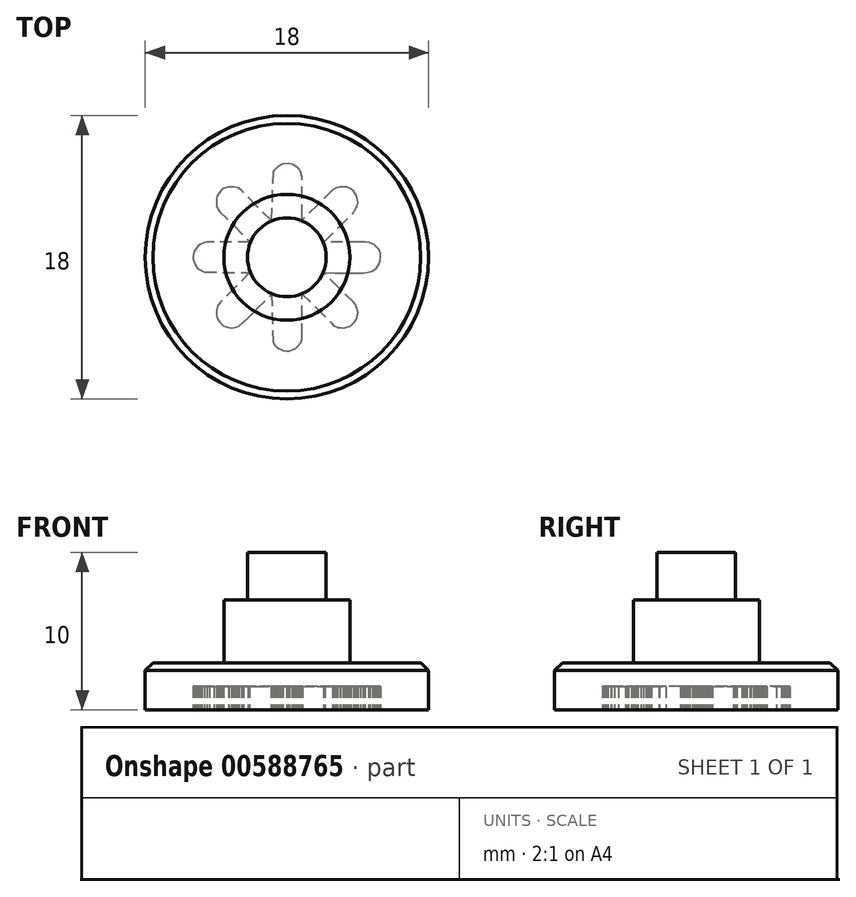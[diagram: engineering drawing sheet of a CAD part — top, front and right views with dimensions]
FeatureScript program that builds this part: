
annotation { "Feature Type Name" : "Feature", "Feature Type Description" : "" }
export const myFeature = defineFeature(function(context is Context, id is Id, definition is map)
    precondition{}
    {
        {
            var Q0;
            Q0=qCreatedBy(makeId("Top.planeOp"),FACE);
            var sketch = newSketch(context, id + "F0", { "sketchPlane" : qUnion([Q0])});
            skCircle(sketch, "E0", {"center": v(0, 0) * mm, "radius": 9 * mm});
            skSolve(sketch);
        }
        {
            var Q0;
            Q0=makeQuery(id+"F0.imprint","IMPRINT",FACE,{"disambiguationData":[TD([[makeQuery(id+"F0.imprint","IMPRINT",EDGE,{"derivedFrom":sQuery(id+"F0.wireOp",EDGE,"E0")}),1.0]])]});
            extrude(context, id + "F1", {"entities" : qUnion([Q0]), "depth" : 3 * mm, "offsetDistance" : 25 * mm});
        }
        {
            var Q0;
            Q0=makeQuery(id+"F1.opExtrude","CAP_EDGE",EDGE,{"disambiguationData":[OSD([sQuery(id+"F0.wireOp",EDGE,"E0")])],"isStart":false});
            chamfer(context, id + "F2", {"entities" : qUnion([Q0]), "width" : .5 * mm, "tangentPropagation" : true});
        }
        {
            var Q0;
            Q0=makeQuery(id+"F1.opExtrude","CAP_FACE",FACE,{"disambiguationData":[OSD([sQuery(id+"F0.wireOp",EDGE,"E0")])],"isStart":false});
            var sketch = newSketch(context, id + "F3", { "sketchPlane" : qUnion([Q0])});
            skCircle(sketch, "E1", {"center": v(0, 0) * mm, "radius": 4 * mm});
            skSolve(sketch);
        }
        {
            var Q0;
            Q0=qSketchRegion(id+"F3",true);
            extrude(context, id + "F4", {"entities" : qUnion([Q0]), "operationType" : NewBodyOperationType.ADD, "depth" : 4 * mm, "offsetDistance" : 25 * mm});
        }
        {
            var Q0;
            Q0=makeQuery(id+"F4.opExtrude","CAP_FACE",FACE,{"disambiguationData":[OSD([sQuery(id+"F3.wireOp",EDGE,"E1")])],"isStart":false});
            var sketch = newSketch(context, id + "F5", { "sketchPlane" : qUnion([Q0])});
            skCircle(sketch, "E2", {"center": v(0, 0) * mm, "radius": 2.5 * mm});
            skSolve(sketch);
        }
        {
            var Q0;
            Q0=qSketchRegion(id+"F5",true);
            extrude(context, id + "F6", {"entities" : qUnion([Q0]), "operationType" : NewBodyOperationType.ADD, "depth" : 3 * mm, "offsetDistance" : 25 * mm});
        }
        {
            var Q0;
            Q0=makeQuery(id+"F1.opExtrude","CAP_FACE",FACE,{"disambiguationData":[OSD([sQuery(id+"F0.wireOp",EDGE,"E0")])],"isStart":true});
            var sketch = newSketch(context, id + "F7", { "sketchPlane" : qUnion([Q0])});
            skLineSegment(sketch, "E3", {"start": v(-0.24, 5.92) * mm, "end": v(-0.03, 5.95) * mm});
            skLineSegment(sketch, "E4", {"start": v(-0.03, 5.95) * mm, "end": v(0.18, 5.95) * mm});
            skLineSegment(sketch, "E5", {"start": v(0.18, 5.95) * mm, "end": v(0.31, 5.9) * mm});
            skLineSegment(sketch, "E6", {"start": v(0.31, 5.9) * mm, "end": v(0.44, 5.83) * mm});
            skLineSegment(sketch, "E7", {"start": v(0.44, 5.83) * mm, "end": v(0.47, 5.81) * mm});
            skLineSegment(sketch, "E8", {"start": v(0.47, 5.81) * mm, "end": v(0.5, 5.8) * mm});
            skLineSegment(sketch, "E9", {"start": v(0.5, 5.8) * mm, "end": v(0.54, 5.8) * mm});
            skLineSegment(sketch, "E10", {"start": v(0.54, 5.8) * mm, "end": v(0.58, 5.77) * mm});
            skLineSegment(sketch, "E11", {"start": v(0.58, 5.77) * mm, "end": v(0.65, 5.71) * mm});
            skLineSegment(sketch, "E12", {"start": v(0.65, 5.71) * mm, "end": v(0.89, 5.42) * mm});
            skLineSegment(sketch, "E13", {"start": v(0.89, 5.42) * mm, "end": v(0.95, 5.19) * mm});
            skLineSegment(sketch, "E14", {"start": v(0.95, 5.19) * mm, "end": v(0.97, 4.95) * mm});
            skLineSegment(sketch, "E15", {"start": v(0.97, 4.95) * mm, "end": v(0.97, 3.1) * mm});
            skLineSegment(sketch, "E16", {"start": v(0.97, 3.1) * mm, "end": v(0.97, 2.33) * mm});
            skLineSegment(sketch, "E17", {"start": v(0.97, 2.33) * mm, "end": v(1.92, 3.27) * mm});
            skLineSegment(sketch, "E18", {"start": v(1.92, 3.27) * mm, "end": v(2.86, 4.21) * mm});
            skLineSegment(sketch, "E19", {"start": v(2.86, 4.21) * mm, "end": v(2.94, 4.3) * mm});
            skLineSegment(sketch, "E20", {"start": v(2.94, 4.3) * mm, "end": v(3.04, 4.36) * mm});
            skLineSegment(sketch, "E21", {"start": v(3.04, 4.36) * mm, "end": v(3.19, 4.42) * mm});
            skLineSegment(sketch, "E22", {"start": v(3.19, 4.42) * mm, "end": v(3.22, 4.45) * mm});
            skLineSegment(sketch, "E23", {"start": v(3.22, 4.45) * mm, "end": v(3.4, 4.48) * mm});
            skLineSegment(sketch, "E24", {"start": v(3.4, 4.48) * mm, "end": v(3.56, 4.48) * mm});
            skLineSegment(sketch, "E25", {"start": v(3.56, 4.48) * mm, "end": v(3.72, 4.48) * mm});
            skLineSegment(sketch, "E26", {"start": v(3.72, 4.48) * mm, "end": v(4.04, 4.36) * mm});
            skLineSegment(sketch, "E27", {"start": v(4.04, 4.36) * mm, "end": v(4.3, 4.12) * mm});
            skLineSegment(sketch, "E28", {"start": v(4.3, 4.12) * mm, "end": v(4.39, 3.98) * mm});
            skLineSegment(sketch, "E29", {"start": v(4.39, 3.98) * mm, "end": v(4.44, 3.83) * mm});
            skLineSegment(sketch, "E30", {"start": v(4.44, 3.83) * mm, "end": v(4.51, 3.5) * mm});
            skLineSegment(sketch, "E31", {"start": v(4.51, 3.5) * mm, "end": v(4.45, 3.2) * mm});
            skLineSegment(sketch, "E32", {"start": v(4.45, 3.2) * mm, "end": v(4.4, 3.12) * mm});
            skLineSegment(sketch, "E33", {"start": v(4.4, 3.12) * mm, "end": v(4.38, 3.05) * mm});
            skLineSegment(sketch, "E34", {"start": v(4.38, 3.05) * mm, "end": v(4.34, 2.98) * mm});
            skLineSegment(sketch, "E35", {"start": v(4.34, 2.98) * mm, "end": v(4.22, 2.86) * mm});
            skLineSegment(sketch, "E36", {"start": v(4.22, 2.86) * mm, "end": v(3.27, 1.91) * mm});
            skLineSegment(sketch, "E37", {"start": v(3.27, 1.91) * mm, "end": v(2.33, 0.97) * mm});
            skLineSegment(sketch, "E38", {"start": v(2.33, 0.97) * mm, "end": v(3.05, 0.98) * mm});
            skLineSegment(sketch, "E39", {"start": v(3.05, 0.98) * mm, "end": v(3.77, 1.01) * mm});
            skLineSegment(sketch, "E40", {"start": v(3.77, 1.01) * mm, "end": v(4.48, 1.01) * mm});
            skLineSegment(sketch, "E41", {"start": v(4.48, 1.01) * mm, "end": v(4.84, 0.99) * mm});
            skLineSegment(sketch, "E42", {"start": v(4.84, 0.99) * mm, "end": v(5.2, 0.94) * mm});
            skLineSegment(sketch, "E43", {"start": v(5.2, 0.94) * mm, "end": v(5.43, 0.88) * mm});
            skLineSegment(sketch, "E44", {"start": v(5.43, 0.88) * mm, "end": v(5.6, 0.74) * mm});
            skLineSegment(sketch, "E45", {"start": v(5.6, 0.74) * mm, "end": v(5.69, 0.67) * mm});
            skLineSegment(sketch, "E46", {"start": v(5.69, 0.67) * mm, "end": v(5.76, 0.6) * mm});
            skLineSegment(sketch, "E47", {"start": v(5.76, 0.6) * mm, "end": v(5.87, 0.41) * mm});
            skLineSegment(sketch, "E48", {"start": v(5.87, 0.41) * mm, "end": v(5.93, 0.23) * mm});
            skLineSegment(sketch, "E49", {"start": v(5.93, 0.23) * mm, "end": v(5.96, 0.04) * mm});
            skLineSegment(sketch, "E50", {"start": v(5.96, 0.04) * mm, "end": v(5.95, -0.15) * mm});
            skLineSegment(sketch, "E51", {"start": v(5.95, -0.15) * mm, "end": v(5.93, -0.24) * mm});
            skLineSegment(sketch, "E52", {"start": v(5.93, -0.24) * mm, "end": v(5.9, -0.32) * mm});
            skLineSegment(sketch, "E53", {"start": v(5.9, -0.32) * mm, "end": v(5.88, -0.4) * mm});
            skLineSegment(sketch, "E54", {"start": v(5.88, -0.4) * mm, "end": v(5.84, -0.48) * mm});
            skLineSegment(sketch, "E55", {"start": v(5.84, -0.48) * mm, "end": v(5.72, -0.62) * mm});
            skLineSegment(sketch, "E56", {"start": v(5.72, -0.62) * mm, "end": v(5.55, -0.82) * mm});
            skLineSegment(sketch, "E57", {"start": v(5.55, -0.82) * mm, "end": v(5.28, -0.91) * mm});
            skLineSegment(sketch, "E58", {"start": v(5.28, -0.91) * mm, "end": v(5.25, -0.94) * mm});
            skLineSegment(sketch, "E59", {"start": v(5.25, -0.94) * mm, "end": v(4.97, -0.97) * mm});
            skLineSegment(sketch, "E60", {"start": v(4.97, -0.97) * mm, "end": v(4.7, -0.97) * mm});
            skLineSegment(sketch, "E61", {"start": v(4.7, -0.97) * mm, "end": v(2.86, -0.97) * mm});
            skLineSegment(sketch, "E62", {"start": v(2.86, -0.97) * mm, "end": v(2.42, -0.97) * mm});
            skLineSegment(sketch, "E63", {"start": v(2.42, -0.97) * mm, "end": v(2.4, -1) * mm});
            skLineSegment(sketch, "E64", {"start": v(2.4, -1) * mm, "end": v(3.33, -1.94) * mm});
            skLineSegment(sketch, "E65", {"start": v(3.33, -1.94) * mm, "end": v(4.28, -2.89) * mm});
            skLineSegment(sketch, "E66", {"start": v(4.28, -2.89) * mm, "end": v(4.3, -2.95) * mm});
            skLineSegment(sketch, "E67", {"start": v(4.3, -2.95) * mm, "end": v(4.34, -3) * mm});
            skLineSegment(sketch, "E68", {"start": v(4.34, -3) * mm, "end": v(4.4, -3.11) * mm});
            skLineSegment(sketch, "E69", {"start": v(4.4, -3.11) * mm, "end": v(4.44, -3.23) * mm});
            skLineSegment(sketch, "E70", {"start": v(4.44, -3.23) * mm, "end": v(4.51, -3.47) * mm});
            skLineSegment(sketch, "E71", {"start": v(4.51, -3.47) * mm, "end": v(4.43, -3.92) * mm});
            skLineSegment(sketch, "E72", {"start": v(4.43, -3.92) * mm, "end": v(4.22, -4.21) * mm});
            skLineSegment(sketch, "E73", {"start": v(4.22, -4.21) * mm, "end": v(4.07, -4.33) * mm});
            skLineSegment(sketch, "E74", {"start": v(4.07, -4.33) * mm, "end": v(3.94, -4.4) * mm});
            skLineSegment(sketch, "E75", {"start": v(3.94, -4.4) * mm, "end": v(3.8, -4.45) * mm});
            skLineSegment(sketch, "E76", {"start": v(3.8, -4.45) * mm, "end": v(3.69, -4.48) * mm});
            skLineSegment(sketch, "E77", {"start": v(3.69, -4.48) * mm, "end": v(3.36, -4.48) * mm});
            skLineSegment(sketch, "E78", {"start": v(3.36, -4.48) * mm, "end": v(3.12, -4.39) * mm});
            skLineSegment(sketch, "E79", {"start": v(3.12, -4.39) * mm, "end": v(2.9, -4.27) * mm});
            skLineSegment(sketch, "E80", {"start": v(2.9, -4.27) * mm, "end": v(1.95, -3.33) * mm});
            skLineSegment(sketch, "E81", {"start": v(1.95, -3.33) * mm, "end": v(1, -2.39) * mm});
            skLineSegment(sketch, "E82", {"start": v(1, -2.39) * mm, "end": v(0.98, -2.43) * mm});
            skLineSegment(sketch, "E83", {"start": v(0.98, -2.43) * mm, "end": v(0.97, -2.48) * mm});
            skLineSegment(sketch, "E84", {"start": v(0.97, -2.48) * mm, "end": v(0.97, -2.6) * mm});
            skLineSegment(sketch, "E85", {"start": v(0.97, -2.6) * mm, "end": v(0.97, -4.42) * mm});
            skLineSegment(sketch, "E86", {"start": v(0.97, -4.42) * mm, "end": v(0.97, -5.1) * mm});
            skLineSegment(sketch, "E87", {"start": v(0.97, -5.1) * mm, "end": v(0.86, -5.45) * mm});
            skLineSegment(sketch, "E88", {"start": v(0.86, -5.45) * mm, "end": v(0.8, -5.56) * mm});
            skLineSegment(sketch, "E89", {"start": v(0.8, -5.56) * mm, "end": v(0.75, -5.61) * mm});
            skLineSegment(sketch, "E90", {"start": v(0.75, -5.61) * mm, "end": v(0.7, -5.65) * mm});
            skLineSegment(sketch, "E91", {"start": v(0.7, -5.65) * mm, "end": v(0.38, -5.89) * mm});
            skLineSegment(sketch, "E92", {"start": v(0.38, -5.89) * mm, "end": v(0.09, -5.95) * mm});
            skLineSegment(sketch, "E93", {"start": v(0.09, -5.95) * mm, "end": v(-0.24, -5.92) * mm});
            skLineSegment(sketch, "E94", {"start": v(-0.24, -5.92) * mm, "end": v(-0.34, -5.89) * mm});
            skLineSegment(sketch, "E95", {"start": v(-0.34, -5.89) * mm, "end": v(-0.44, -5.83) * mm});
            skLineSegment(sketch, "E96", {"start": v(-0.44, -5.83) * mm, "end": v(-0.5, -5.8) * mm});
            skLineSegment(sketch, "E97", {"start": v(-0.5, -5.8) * mm, "end": v(-0.56, -5.77) * mm});
            skLineSegment(sketch, "E98", {"start": v(-0.56, -5.77) * mm, "end": v(-0.7, -5.65) * mm});
            skLineSegment(sketch, "E99", {"start": v(-0.7, -5.65) * mm, "end": v(-0.83, -5.5) * mm});
            skLineSegment(sketch, "E100", {"start": v(-0.83, -5.5) * mm, "end": v(-0.88, -5.42) * mm});
            skLineSegment(sketch, "E101", {"start": v(-0.88, -5.42) * mm, "end": v(-1, -2.36) * mm});
            skLineSegment(sketch, "E102", {"start": v(-1, -2.36) * mm, "end": v(-1.95, -3.3) * mm});
            skLineSegment(sketch, "E103", {"start": v(-1.95, -3.3) * mm, "end": v(-2.9, -4.24) * mm});
            skLineSegment(sketch, "E104", {"start": v(-2.9, -4.24) * mm, "end": v(-3.07, -4.39) * mm});
            skLineSegment(sketch, "E105", {"start": v(-3.07, -4.39) * mm, "end": v(-3.4, -4.48) * mm});
            skLineSegment(sketch, "E106", {"start": v(-3.4, -4.48) * mm, "end": v(-3.72, -4.48) * mm});
            skLineSegment(sketch, "E107", {"start": v(-3.72, -4.48) * mm, "end": v(-4.01, -4.36) * mm});
            skLineSegment(sketch, "E108", {"start": v(-4.01, -4.36) * mm, "end": v(-4.1, -4.3) * mm});
            skLineSegment(sketch, "E109", {"start": v(-4.1, -4.3) * mm, "end": v(-4.19, -4.24) * mm});
            skLineSegment(sketch, "E110", {"start": v(-4.19, -4.24) * mm, "end": v(-4.3, -4.1) * mm});
            skLineSegment(sketch, "E111", {"start": v(-4.3, -4.1) * mm, "end": v(-4.37, -4) * mm});
            skLineSegment(sketch, "E112", {"start": v(-4.37, -4) * mm, "end": v(-4.42, -3.89) * mm});
            skLineSegment(sketch, "E113", {"start": v(-4.42, -3.89) * mm, "end": v(-4.46, -3.76) * mm});
            skLineSegment(sketch, "E114", {"start": v(-4.46, -3.76) * mm, "end": v(-4.48, -3.62) * mm});
            skLineSegment(sketch, "E115", {"start": v(-4.48, -3.62) * mm, "end": v(-4.48, -3.42) * mm});
            skLineSegment(sketch, "E116", {"start": v(-4.48, -3.42) * mm, "end": v(-4.45, -3.2) * mm});
            skLineSegment(sketch, "E117", {"start": v(-4.45, -3.2) * mm, "end": v(-4.42, -3.16) * mm});
            skLineSegment(sketch, "E118", {"start": v(-4.42, -3.16) * mm, "end": v(-4.4, -3.1) * mm});
            skLineSegment(sketch, "E119", {"start": v(-4.4, -3.1) * mm, "end": v(-4.34, -3) * mm});
            skLineSegment(sketch, "E120", {"start": v(-4.34, -3) * mm, "end": v(-4.28, -2.92) * mm});
            skLineSegment(sketch, "E121", {"start": v(-4.28, -2.92) * mm, "end": v(-3.33, -1.97) * mm});
            skLineSegment(sketch, "E122", {"start": v(-3.33, -1.97) * mm, "end": v(-2.39, -1.03) * mm});
            skLineSegment(sketch, "E123", {"start": v(-2.39, -1.03) * mm, "end": v(-2.37, -1) * mm});
            skLineSegment(sketch, "E124", {"start": v(-2.37, -1) * mm, "end": v(-2.36, -0.97) * mm});
            skLineSegment(sketch, "E125", {"start": v(-2.36, -0.97) * mm, "end": v(-4.19, -0.97) * mm});
            skLineSegment(sketch, "E126", {"start": v(-4.19, -0.97) * mm, "end": v(-4.63, -0.97) * mm});
            skLineSegment(sketch, "E127", {"start": v(-4.63, -0.97) * mm, "end": v(-4.93, -0.98) * mm});
            skLineSegment(sketch, "E128", {"start": v(-4.93, -0.98) * mm, "end": v(-5.08, -0.97) * mm});
            skLineSegment(sketch, "E129", {"start": v(-5.08, -0.97) * mm, "end": v(-5.22, -0.94) * mm});
            skLineSegment(sketch, "E130", {"start": v(-5.22, -0.94) * mm, "end": v(-5.52, -0.82) * mm});
            skLineSegment(sketch, "E131", {"start": v(-5.52, -0.82) * mm, "end": v(-5.66, -0.7) * mm});
            skLineSegment(sketch, "E132", {"start": v(-5.66, -0.7) * mm, "end": v(-5.78, -0.56) * mm});
            skLineSegment(sketch, "E133", {"start": v(-5.78, -0.56) * mm, "end": v(-5.84, -0.46) * mm});
            skLineSegment(sketch, "E134", {"start": v(-5.84, -0.46) * mm, "end": v(-5.9, -0.35) * mm});
            skLineSegment(sketch, "E135", {"start": v(-5.9, -0.35) * mm, "end": v(-5.94, -0.2) * mm});
            skLineSegment(sketch, "E136", {"start": v(-5.94, -0.2) * mm, "end": v(-5.96, -0.06) * mm});
            skLineSegment(sketch, "E137", {"start": v(-5.96, -0.06) * mm, "end": v(-5.96, 0.12) * mm});
            skLineSegment(sketch, "E138", {"start": v(-5.96, 0.12) * mm, "end": v(-5.84, 0.47) * mm});
            skLineSegment(sketch, "E139", {"start": v(-5.84, 0.47) * mm, "end": v(-5.66, 0.7) * mm});
            skLineSegment(sketch, "E140", {"start": v(-5.66, 0.7) * mm, "end": v(-5.61, 0.76) * mm});
            skLineSegment(sketch, "E141", {"start": v(-5.61, 0.76) * mm, "end": v(-5.56, 0.8) * mm});
            skLineSegment(sketch, "E142", {"start": v(-5.56, 0.8) * mm, "end": v(-5.43, 0.85) * mm});
            skLineSegment(sketch, "E143", {"start": v(-5.43, 0.85) * mm, "end": v(-5.4, 0.88) * mm});
            skLineSegment(sketch, "E144", {"start": v(-5.4, 0.88) * mm, "end": v(-5.22, 0.94) * mm});
            skLineSegment(sketch, "E145", {"start": v(-5.22, 0.94) * mm, "end": v(-2.36, 0.97) * mm});
            skLineSegment(sketch, "E146", {"start": v(-2.36, 0.97) * mm, "end": v(-3.3, 1.91) * mm});
            skLineSegment(sketch, "E147", {"start": v(-3.3, 1.91) * mm, "end": v(-4.25, 2.89) * mm});
            skLineSegment(sketch, "E148", {"start": v(-4.25, 2.89) * mm, "end": v(-4.4, 3.1) * mm});
            skLineSegment(sketch, "E149", {"start": v(-4.4, 3.1) * mm, "end": v(-4.48, 3.36) * mm});
            skLineSegment(sketch, "E150", {"start": v(-4.48, 3.36) * mm, "end": v(-4.48, 3.71) * mm});
            skLineSegment(sketch, "E151", {"start": v(-4.48, 3.71) * mm, "end": v(-4.4, 3.93) * mm});
            skLineSegment(sketch, "E152", {"start": v(-4.4, 3.93) * mm, "end": v(-4.35, 4.03) * mm});
            skLineSegment(sketch, "E153", {"start": v(-4.35, 4.03) * mm, "end": v(-4.28, 4.12) * mm});
            skLineSegment(sketch, "E154", {"start": v(-4.28, 4.12) * mm, "end": v(-4.01, 4.36) * mm});
            skLineSegment(sketch, "E155", {"start": v(-4.01, 4.36) * mm, "end": v(-3.69, 4.48) * mm});
            skLineSegment(sketch, "E156", {"start": v(-3.69, 4.48) * mm, "end": v(-3.52, 4.49) * mm});
            skLineSegment(sketch, "E157", {"start": v(-3.52, 4.49) * mm, "end": v(-3.36, 4.48) * mm});
            skLineSegment(sketch, "E158", {"start": v(-3.36, 4.48) * mm, "end": v(-3.2, 4.42) * mm});
            skLineSegment(sketch, "E159", {"start": v(-3.2, 4.42) * mm, "end": v(-3.04, 4.36) * mm});
            skLineSegment(sketch, "E160", {"start": v(-3.04, 4.36) * mm, "end": v(-2.75, 4.1) * mm});
            skLineSegment(sketch, "E161", {"start": v(-2.75, 4.1) * mm, "end": v(-2.46, 3.84) * mm});
            skLineSegment(sketch, "E162", {"start": v(-2.46, 3.84) * mm, "end": v(-1.92, 3.3) * mm});
            skLineSegment(sketch, "E163", {"start": v(-1.92, 3.3) * mm, "end": v(-0.97, 2.36) * mm});
            skLineSegment(sketch, "E164", {"start": v(-0.97, 2.36) * mm, "end": v(-0.88, 5.39) * mm});
            skLineSegment(sketch, "E165", {"start": v(-0.88, 5.39) * mm, "end": v(-0.77, 5.6) * mm});
            skLineSegment(sketch, "E166", {"start": v(-0.77, 5.6) * mm, "end": v(-0.71, 5.64) * mm});
            skLineSegment(sketch, "E167", {"start": v(-0.71, 5.64) * mm, "end": v(-0.65, 5.68) * mm});
            skLineSegment(sketch, "E168", {"start": v(-0.65, 5.68) * mm, "end": v(-0.5, 5.8) * mm});
            skLineSegment(sketch, "E169", {"start": v(-0.5, 5.8) * mm, "end": v(-0.37, 5.87) * mm});
            skLineSegment(sketch, "E170", {"start": v(-0.37, 5.87) * mm, "end": v(-0.24, 5.92) * mm});
            skSolve(sketch);
        }
        {
            var Q0;
            Q0 = qSketchRegion(id + "F7", true);
            extrude(context, id + "F8", {"entities" : qUnion([Q0]), "operationType" : NewBodyOperationType.REMOVE, "oppositeDirection" : true, "depth" : 1.5 * mm, "offsetDistance" : 25 * mm});
        }
    });
